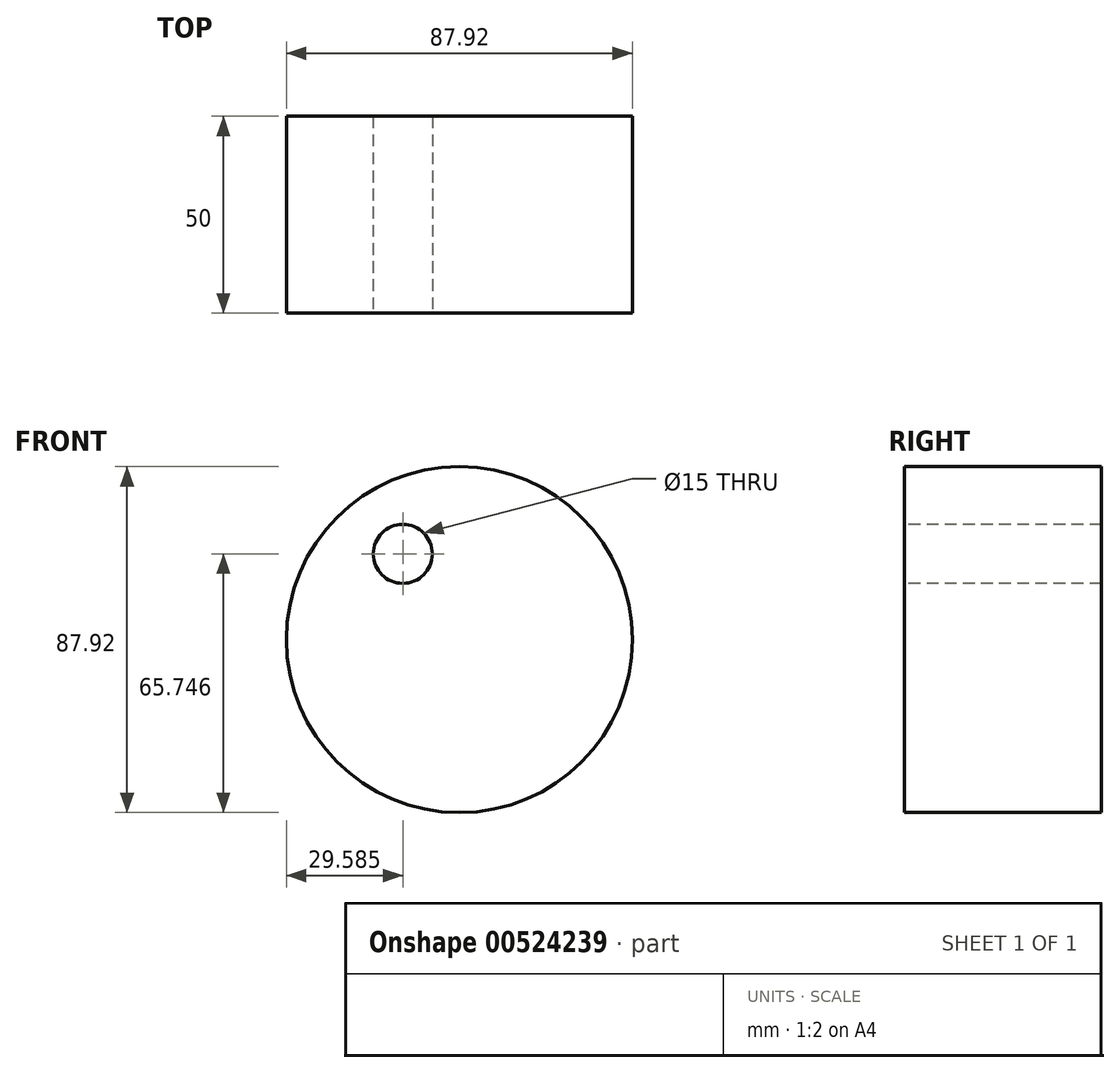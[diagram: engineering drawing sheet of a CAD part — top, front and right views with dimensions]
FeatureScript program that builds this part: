
annotation { "Feature Type Name" : "Feature", "Feature Type Description" : "" }
export const myFeature = defineFeature(function(context is Context, id is Id, definition is map)
    precondition{}
    {
        {
            var Q0;
            Q0=qCreatedBy(makeId("Front.planeOp"),FACE);
            var sketch = newSketch(context, id + "F0", { "sketchPlane" : qUnion([Q0])});
            skCircle(sketch, "E0", {"center": v(0, 0) * mm, "radius": 43.96 * mm});
            skSolve(sketch);
        }
        {
            var Q0;
            Q0=makeQuery(id+"F0.imprint","IMPRINT",FACE,{"disambiguationData":[TD([[makeQuery(id+"F0.imprint","IMPRINT",EDGE,{"derivedFrom":sQuery(id+"F0.wireOp",EDGE,"E0")}),1.0]])]});
            extrude(context, id + "F1", {"entities" : qUnion([Q0]), "endBound" : BoundingType.SYMMETRIC, "depth" : 50 * mm, "offsetDistance" : 25 * mm});
        }
        {
            var Q0;
            Q0=makeQuery(id+"F1.opExtrude","CAP_FACE",FACE,{"disambiguationData":[OSD([sQuery(id+"F0.wireOp",EDGE,"E0")])],"isStart":false});
            var sketch = newSketch(context, id + "F2", { "sketchPlane" : qUnion([Q0])});
            skPoint(sketch, "E1", {"position": v(-14.38, 21.79) * mm});
            skSolve(sketch);
        }
        {
            var Q0;
            Q0=sQuery(id+"F2.wireOp",VERTEX,"E1");
            var Q1;
            Q1=makeQuery(id+"F1.opExtrude","SWEPT_BODY",BODY,{"disambiguationData":[OSD([sQuery(id+"F0.wireOp",EDGE,"E0")])]});
            hole(context, id + "F3", {"style" : HoleStyle.SIMPLE, "endStyle" : HoleEndStyle.THROUGH, "holeDiameter" : 15 * mm, "isTappedThrough" : true, "tappedDepth" : 12 * mm, "tapClearance" : 3, "locations" : qUnion([Q0]), "scope" : qUnion([Q1])});
        }
    });
